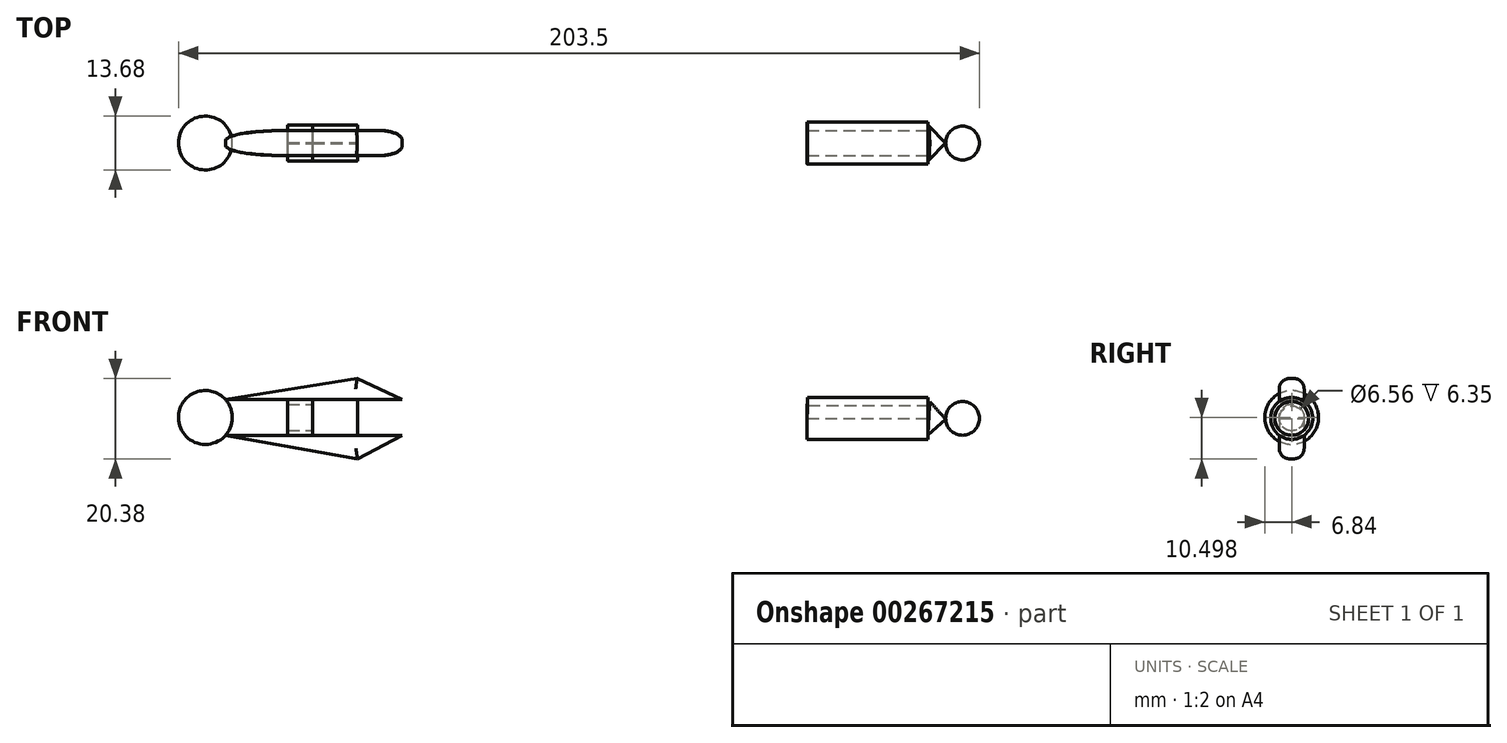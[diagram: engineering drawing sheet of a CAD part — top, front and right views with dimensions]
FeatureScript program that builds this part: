
annotation { "Feature Type Name" : "Feature", "Feature Type Description" : "" }
export const myFeature = defineFeature(function(context is Context, id is Id, definition is map)
    precondition{}
    {
        {
            var Q0;
            Q0=qCreatedBy(makeId("Front.planeOp"),FACE);
            var sketch = newSketch(context, id + "F0", { "sketchPlane" : qUnion([Q0])});
            skLineSegment(sketch, "E0", {"start": v(26.52, 0) * mm, "end": v(57.17, 0) * mm});
            skLineSegment(sketch, "E1", {"start": v(-87.73, 4.52) * mm, "end": v(-87.73, 0) * mm});
            skLineSegment(sketch, "E2", {"start": v(-87.73, 0) * mm, "end": v(26.52, 0) * mm});
            skLineSegment(sketch, "E3", {"start": v(-87.73, -5.98) * mm, "end": v(-87.73, 0) * mm});
            skLineSegment(sketch, "E4", {"start": v(-87.73, -5.98) * mm, "end": v(-121.25, 0) * mm});
            skLineSegment(sketch, "E5", {"start": v(-121.25, 0) * mm, "end": v(-87.73, 0) * mm});
            skLineSegment(sketch, "E6", {"start": v(-99.1, 4.52) * mm, "end": v(-87.73, 4.52) * mm});
            skLineSegment(sketch, "E7", {"start": v(-87.73, 4.52) * mm, "end": v(-99.1, 4.52) * mm});
            skLineSegment(sketch, "E8", {"start": v(-99.1, 0) * mm, "end": v(-87.73, 0) * mm});
            skLineSegment(sketch, "E9", {"start": v(-99.1, 4.52) * mm, "end": v(-99.1, 0) * mm});
            skLineSegment(sketch, "E10", {"start": v(26.52, 4.3) * mm, "end": v(-87.73, 4.52) * mm});
            skLineSegment(sketch, "E11", {"start": v(-99.1, 9.03) * mm, "end": v(-87.83, 9.03) * mm});
            skLineSegment(sketch, "E12", {"start": v(-87.83, 9.03) * mm, "end": v(-87.83, 14.4) * mm});
            skLineSegment(sketch, "E13", {"start": v(-99.1, 9.03) * mm, "end": v(-121.25, 9.03) * mm});
            skLineSegment(sketch, "E14", {"start": v(-121.25, 9.03) * mm, "end": v(-87.83, 14.4) * mm});
            skLineSegment(sketch, "E15", {"start": v(-76.37, 9.03) * mm, "end": v(-87.83, 9.03) * mm});
            skLineSegment(sketch, "E16", {"start": v(-87.83, 14.4) * mm, "end": v(-76.37, 9.03) * mm});
            skLineSegment(sketch, "E17", {"start": v(-87.73, -5.98) * mm, "end": v(-76.37, 0) * mm});
            skLineSegment(sketch, "E18", {"start": v(57.4, 4.3) * mm, "end": v(57.17, 0) * mm});
            skLineSegment(sketch, "E19", {"start": v(26.52, 4.3) * mm, "end": v(57.4, 4.3) * mm});
            skLineSegment(sketch, "E20", {"start": v(26.52, 4.3) * mm, "end": v(26.52, 0) * mm});
            skLineSegment(sketch, "E21", {"start": v(-76.37, 0) * mm, "end": v(-67.04, 0) * mm});
            skArc(sketch, "E22", {"start": v(-133.22, 4.52) * mm, "mid": v(-126.38, -2.32) * mm, "end": v(-119.55, 4.52) * mm});
            skLineSegment(sketch, "E23", {"start": v(-133.22, 4.52) * mm, "end": v(-119.55, 4.52) * mm});
            skLineSegment(sketch, "E24", {"start": v(57.4, 4.3) * mm, "end": v(65.99, 3.81) * mm});
            skLineSegment(sketch, "E25", {"start": v(57.4, 4.3) * mm, "end": v(57.4, 8.59) * mm});
            skLineSegment(sketch, "E26", {"start": v(57.4, 8.59) * mm, "end": v(65.99, 8.59) * mm});
            skLineSegment(sketch, "E27", {"start": v(65.99, 8.59) * mm, "end": v(65.99, 0) * mm});
            skLineSegment(sketch, "E28", {"start": v(65.99, 0) * mm, "end": v(57.17, 0) * mm});
            skArc(sketch, "E29", {"start": v(65.99, 0) * mm, "mid": v(70.28, 4.3) * mm, "end": v(65.99, 8.59) * mm});
            skLineSegment(sketch, "E30", {"start": v(61.7, 4.05) * mm, "end": v(57.17, 0) * mm});
            skSolve(sketch);
        }
        {
            var Q0;
            Q0=sQuery(id+"F0.wireOp",EDGE,"E2");
            var Q1;
            Q1=sQuery(id+"F0.wireOp",EDGE,"E10");
            revolve(context, id + "F1", {"bodyType" : ToolBodyType.SURFACE, "surfaceEntities" : qUnion([Q0]), "axis" : qUnion([Q1]), "revolveType" : RevolveType.FULL});
        }
        {
            var Q0;
            Q0=makeQuery(id+"F0.imprint","IMPRINT",FACE,{"disambiguationData":[TD([[makeQuery(id+"F0.imprint","IMPRINT",EDGE,{"derivedFrom":sQuery(id+"F0.wireOp",EDGE,"E1")}),-1.0]])]});
            var Q1;
            Q1=sQuery(id+"F0.wireOp",EDGE,"E7");
            revolve(context, id + "F2", {"entities" : qUnion([Q0]), "axis" : qUnion([Q1]), "revolveType" : RevolveType.FULL});
        }
        {
            var Q0;
            {var subQ3=sQuery(id+"F0.wireOp",EDGE,"E0");Q0=makeQuery(id+"F0.imprint","IMPRINT",FACE,{"disambiguationData":[TD([[makeQuery(id+"F0.imprint","IMPRINT",EDGE,{"derivedFrom":subQ3}),1.0]])]});}
            extrude(context, id + "F3", {"entities" : qUnion([Q0]), "depth" : 6.35 * mm, "symmetric" : true});
        }
        {
            var Q0;
            Q0=makeQuery(id+"F0.imprint","IMPRINT",FACE,{"disambiguationData":[TD([[makeQuery(id+"F0.imprint","IMPRINT",EDGE,{"derivedFrom":sQuery(id+"F0.wireOp",EDGE,"E3")}),1.0]])]});
            extrude(context, id + "F4", {"entities" : qUnion([Q0]), "operationType" : NewBodyOperationType.ADD, "depth" : 6.35 * mm, "symmetric" : true});
        }
        {
            var Q0;
            Q0=makeQuery(id+"F0.imprint","IMPRINT",FACE,{"disambiguationData":[TD([[makeQuery(id+"F0.imprint","IMPRINT",EDGE,{"derivedFrom":sQuery(id+"F0.wireOp",EDGE,"E11")}),1.0]])]});
            extrude(context, id + "F5", {"entities" : qUnion([Q0]), "operationType" : NewBodyOperationType.ADD, "depth" : 6.35 * mm, "symmetric" : true});
        }
        {
            var Q0;
            Q0=makeQuery(id+"F0.imprint","IMPRINT",FACE,{"disambiguationData":[TD([[makeQuery(id+"F0.imprint","IMPRINT",EDGE,{"derivedFrom":sQuery(id+"F0.wireOp",EDGE,"E12")}),-1.0]])]});
            extrude(context, id + "F6", {"entities" : qUnion([Q0]), "operationType" : NewBodyOperationType.ADD, "depth" : 6.35 * mm, "symmetric" : true});
        }
        {
            var Q0;
            {var subQ0=sQuery(id+"F0.wireOp",EDGE,"E3");Q0=makeQuery(id+"F0.imprint","IMPRINT",FACE,{"disambiguationData":[TD([[makeQuery(id+"F0.imprint","IMPRINT",EDGE,{"derivedFrom":subQ0}),-1.0]])]});}
            extrude(context, id + "F7", {"entities" : qUnion([Q0]), "operationType" : NewBodyOperationType.ADD, "depth" : 6.35 * mm, "symmetric" : true});
        }
        {
            var Q0;
            Q0=makeQuery(id+"F2.opRevolve","SWEPT_FACE",FACE,{"disambiguationData":[OSD([sQuery(id+"F0.wireOp",EDGE,"E9")])]});
            var sketch = newSketch(context, id + "F8", { "sketchPlane" : qUnion([Q0])});
            skCircle(sketch, "E31", {"center": v(0, 4.52) * mm, "radius": 3.28 * mm});
            skSolve(sketch);
        }
        {
            var Q0;
            Q0=makeQuery(id+"F8.imprint","IMPRINT",FACE,{"disambiguationData":[TD([[makeQuery(id+"F8.imprint","IMPRINT",EDGE,{"derivedFrom":sQuery(id+"F8.wireOp",EDGE,"E31")}),-1.0]])]});
            extrude(context, id + "F9", {"entities" : qUnion([Q0]), "depth" : 6.35 * mm});
        }
        {
            var Q0;
            Q0=makeQuery(id+"F3.opExtrude","CAP_FACE",FACE,{"disambiguationData":[OSD([sQuery(id+"F0.wireOp",EDGE,"E0"),sQuery(id+"F0.wireOp",EDGE,"E18"),sQuery(id+"F0.wireOp",EDGE,"E19"),sQuery(id+"F0.wireOp",EDGE,"E20")])],"isStart":false});
            var Q1;
            Q1=sQuery(id+"F0.wireOp",EDGE,"E19");
            revolve(context, id + "F10", {"operationType" : NewBodyOperationType.ADD, "entities" : qUnion([Q0]), "axis" : qUnion([Q1]), "revolveType" : RevolveType.FULL});
        }
        {
            var Q0;
            {var subQ2=sQuery(id+"F0.wireOp",EDGE,"E23");Q0=makeQuery(id+"F0.imprint","IMPRINT",FACE,{"disambiguationData":[TD([[makeQuery(id+"F0.imprint","IMPRINT",EDGE,{"derivedFrom":subQ2}),-1.0]])]});}
            var Q1;
            Q1=sQuery(id+"F0.wireOp",EDGE,"E23");
            revolve(context, id + "F11", {"operationType" : NewBodyOperationType.ADD, "entities" : qUnion([Q0]), "axis" : qUnion([Q1]), "revolveType" : RevolveType.FULL});
        }
        {
            var Q0;
            Q0=makeQuery(id+"F5.opExtrude","CAP_EDGE",EDGE,{"disambiguationData":[OSD([sQuery(id+"F0.wireOp",EDGE,"E14")])],"isStart":true});
            var Q1;
            Q1=makeQuery(id+"F5.opExtrude","CAP_EDGE",EDGE,{"disambiguationData":[OSD([sQuery(id+"F0.wireOp",EDGE,"E14")])],"isStart":false});
            var Q2;
            Q2=makeQuery(id+"F6.opExtrude","CAP_EDGE",EDGE,{"disambiguationData":[OSD([sQuery(id+"F0.wireOp",EDGE,"E16")])],"isStart":true});
            var Q3;
            Q3=makeQuery(id+"F6.opExtrude","CAP_EDGE",EDGE,{"disambiguationData":[OSD([sQuery(id+"F0.wireOp",EDGE,"E16")])],"isStart":false});
            var Q4;
            Q4=makeQuery(id+"F4.opExtrude","CAP_EDGE",EDGE,{"disambiguationData":[OSD([sQuery(id+"F0.wireOp",EDGE,"E4")])],"isStart":true});
            var Q5;
            Q5=makeQuery(id+"F7.opExtrude","CAP_EDGE",EDGE,{"disambiguationData":[OSD([sQuery(id+"F0.wireOp",EDGE,"E17")])],"isStart":true});
            var Q6;
            Q6=makeQuery(id+"F7.opExtrude","CAP_EDGE",EDGE,{"disambiguationData":[OSD([sQuery(id+"F0.wireOp",EDGE,"E17")])],"isStart":false});
            var Q7;
            Q7=makeQuery(id+"F4.opExtrude","CAP_EDGE",EDGE,{"disambiguationData":[OSD([sQuery(id+"F0.wireOp",EDGE,"E4")])],"isStart":false});
            fillet(context, id + "F12", {"entities" : qUnion([Q0, Q1, Q2, Q3, Q4, Q5, Q6, Q7]), "radius" : 2.54 * mm, "tangentPropagation" : true, "allowEdgeOverflow" : false});
        }
        {
            var Q0;
            {var subQ2=sQuery(id+"F0.wireOp",EDGE,"E29");Q0=makeQuery(id+"F0.imprint","IMPRINT",FACE,{"disambiguationData":[TD([[makeQuery(id+"F0.imprint","IMPRINT",EDGE,{"derivedFrom":subQ2}),1.0]])]});}
            var Q1;
            Q1=sQuery(id+"F0.wireOp",EDGE,"E27");
            revolve(context, id + "F13", {"entities" : qUnion([Q0]), "axis" : qUnion([Q1]), "revolveType" : RevolveType.FULL});
        }
        {
            var Q0;
            {var subQ0=sQuery(id+"F0.wireOp",EDGE,"E18");Q0=makeQuery(id+"F0.imprint","IMPRINT",FACE,{"disambiguationData":[TD([[makeQuery(id+"F0.imprint","IMPRINT",EDGE,{"derivedFrom":subQ0}),1.0]])]});}
            var Q1;
            Q1=sQuery(id+"F0.wireOp",EDGE,"E24");
            revolve(context, id + "F14", {"operationType" : NewBodyOperationType.ADD, "entities" : qUnion([Q0]), "axis" : qUnion([Q1]), "revolveType" : RevolveType.FULL});
        }
    });
